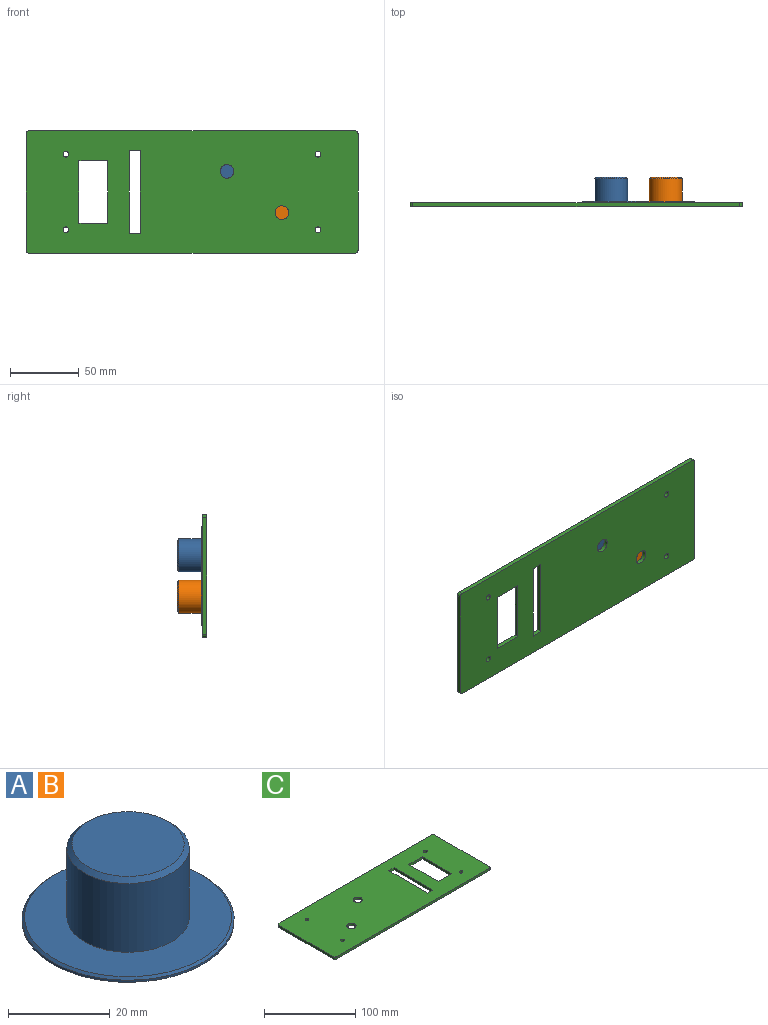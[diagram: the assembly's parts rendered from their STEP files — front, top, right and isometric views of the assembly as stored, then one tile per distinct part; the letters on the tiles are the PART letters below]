
ASSEMBLY  parts=3 mates=2
PART A: 7 faces, bbox 41.6x41.6x18.5 mm
  f0: cylinder r=20.8mm len=41.6mm, axis (0,0,-1), area 65.3mm2, adj f2,f6
  f1: plane 40.6x40.6mm, normal (0,0,1), area 842.2mm2, adj f3,f6
  f2: plane 41.6x41.6mm, normal (0,0,-1), area 1359.2mm2, adj f0
  f3: cylinder r=12mm len=24mm, axis (0,0,-1), area 1244.1mm2, adj f1,f5
  f4: plane 22x22mm, normal (0,0,1), area 380.1mm2, adj f5
  f5: cone r=11mm half-angle=45deg, axis (0,0,-1), area 102.2mm2, adj f3,f4
  f6: cone r=20.3mm half-angle=45deg, axis (0,0,-1), area 91.3mm2, adj f0,f1
PART B: same geometry as A
PART C: 24 faces, bbox 241.3x88.9x3 mm
  f0: plane 84.9x3mm, normal (-1,0,0), area 254.7mm2, adj f1,f21,f22,f23
  f1: cylinder r=2mm len=3mm, axis (0,0,-1), area 9.4mm2, adj f0,f2,f22,f23
  f2: plane 237.3x3mm, normal (0,-1,0), area 711.9mm2, adj f1,f3,f22,f23
  f3: cylinder r=2mm len=3mm, axis (0,0,-1), area 9.4mm2, adj f2,f4,f22,f23
  f4: plane 84.9x3mm, normal (1,0,0), area 254.7mm2, adj f3,f5,f22,f23
  f5: cylinder r=2mm len=3mm, axis (0,0,-1), area 9.4mm2, adj f4,f6,f22,f23
  f6: plane 237.3x3mm, normal (0,1,0), area 711.9mm2, adj f5,f21,f22,f23
  f7: plane 45.5x3mm, normal (1,0,0), area 136.5mm2, adj f8,f13,f22,f23
  f8: plane 21x3mm, normal (0,-1,0), area 63mm2, adj f7,f9,f22,f23
  f9: plane 45.5x3mm, normal (-1,0,0), area 136.5mm2, adj f8,f13,f22,f23
  f10: plane 60x3mm, normal (1,0,0), area 180mm2, adj f11,f14,f22,f23
  f11: plane 8x3mm, normal (0,-1,0), area 24mm2, adj f10,f12,f22,f23
  f12: plane 60x3mm, normal (-1,0,0), area 180mm2, adj f11,f14,f22,f23
  f13: plane 21x3mm, normal (0,1,0), area 63mm2, adj f7,f9,f22,f23
  f14: plane 8x3mm, normal (0,1,0), area 24mm2, adj f10,f12,f22,f23
  f15: cylinder r=2.1mm len=4.2mm, axis (0,0,-1), area 39.6mm2, adj f22,f23
  f16: cylinder r=2.1mm len=4.2mm, axis (0,0,-1), area 39.6mm2, adj f22,f23
  f17: cylinder r=2.1mm len=4.2mm, axis (0,0,-1), area 39.6mm2, adj f22,f23
  f18: cylinder r=5mm len=10mm, axis (0,0,-1), area 94.2mm2, adj f22,f23
  f19: cylinder r=5mm len=10mm, axis (0,0,-1), area 94.2mm2, adj f22,f23
  f20: cylinder r=2.1mm len=4.2mm, axis (0,0,-1), area 39.6mm2, adj f22,f23
  f21: cylinder r=2mm len=3mm, axis (0,0,-1), area 9.4mm2, adj f0,f6,f22,f23
  f22: plane 241.3x88.9mm, normal (0,0,1), area 19800.1mm2, adj f0,f1,f2,f3,f4,f5,f6,f7
  f23: plane 241.3x88.9mm, normal (0,0,-1), area 19800.1mm2, adj f0,f1,f2,f3,f4,f5,f6,f7
PLACE A rot(axis=(-1,0,0),90deg) t=(-93.16,0,57.45)mm
PLACE B rot(axis=(-1,0,0),90deg) t=(-53.3,0,27.45)mm
PLACE C rot(axis=(0,0.71,0.71),180deg) t=(2,-3,-2)mm
MATE fastened B.f0 <-> C.f18  axis (0,-1,0) through (-53.3,0,27.45)mm
MATE fastened A.f0 <-> C.f19  axis (0,-1,0) through (-93.16,0,57.45)mm
